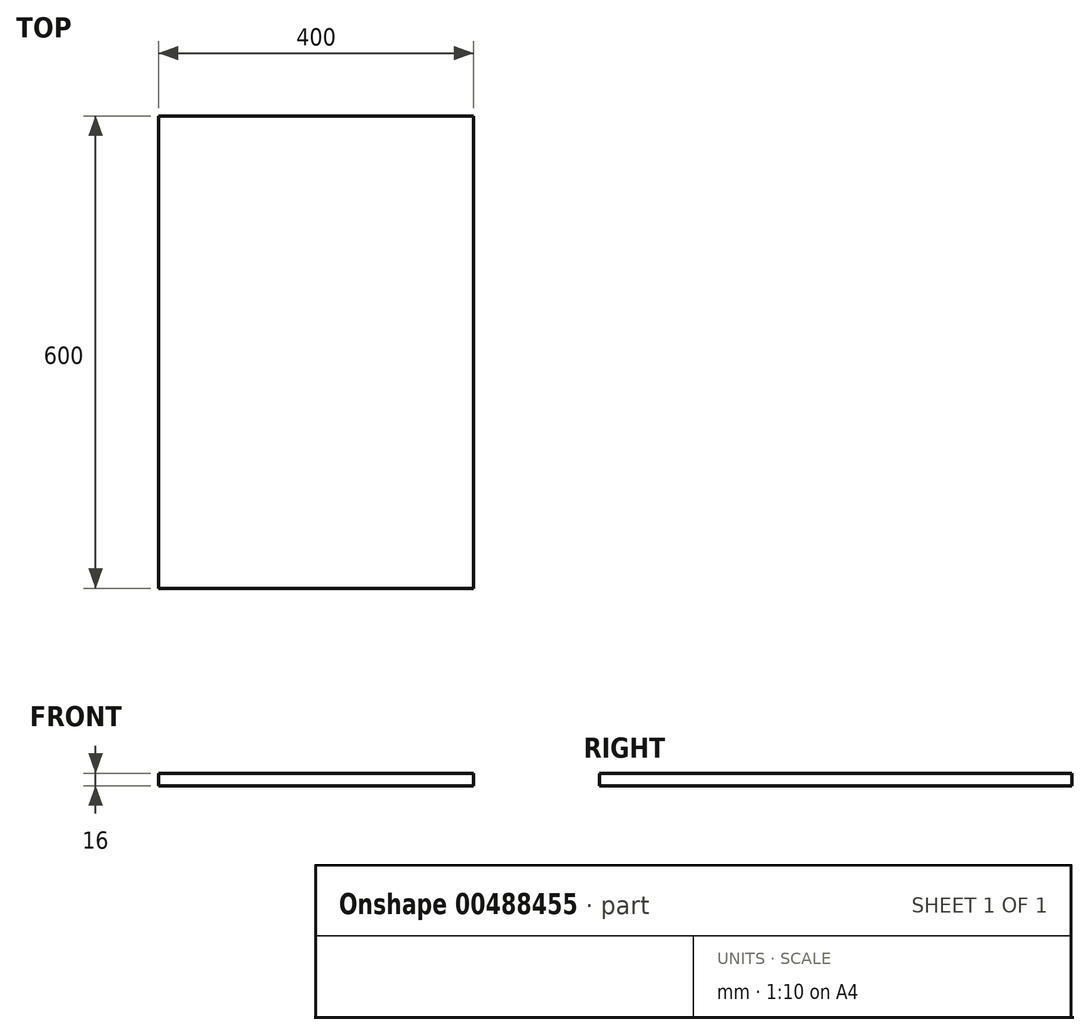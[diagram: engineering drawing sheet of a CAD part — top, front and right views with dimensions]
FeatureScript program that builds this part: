
annotation { "Feature Type Name" : "Feature", "Feature Type Description" : "" }
export const myFeature = defineFeature(function(context is Context, id is Id, definition is map)
    precondition{}
    {
        {
            var Q0;
            Q0=qCreatedBy(makeId("Top.planeOp"),FACE);
            var sketch = newSketch(context, id + "F0", { "sketchPlane" : qUnion([Q0])});
            skLineSegment(sketch, "E0.bottom", {"start": v(0, 0) * mm, "end": v(400, 0) * mm});
            skLineSegment(sketch, "E0.top", {"start": v(0, 600) * mm, "end": v(400, 600) * mm});
            skLineSegment(sketch, "E0.left", {"start": v(0, 0) * mm, "end": v(0, 600) * mm});
            skLineSegment(sketch, "E0.right", {"start": v(400, 0) * mm, "end": v(400, 600) * mm});
            skSolve(sketch);
        }
        {
            var Q0;
            Q0 = qSketchRegion(id + "F0", true);
            extrude(context, id + "F1", {"entities" : qUnion([Q0]), "depth" : 16 * mm});
        }
    });
